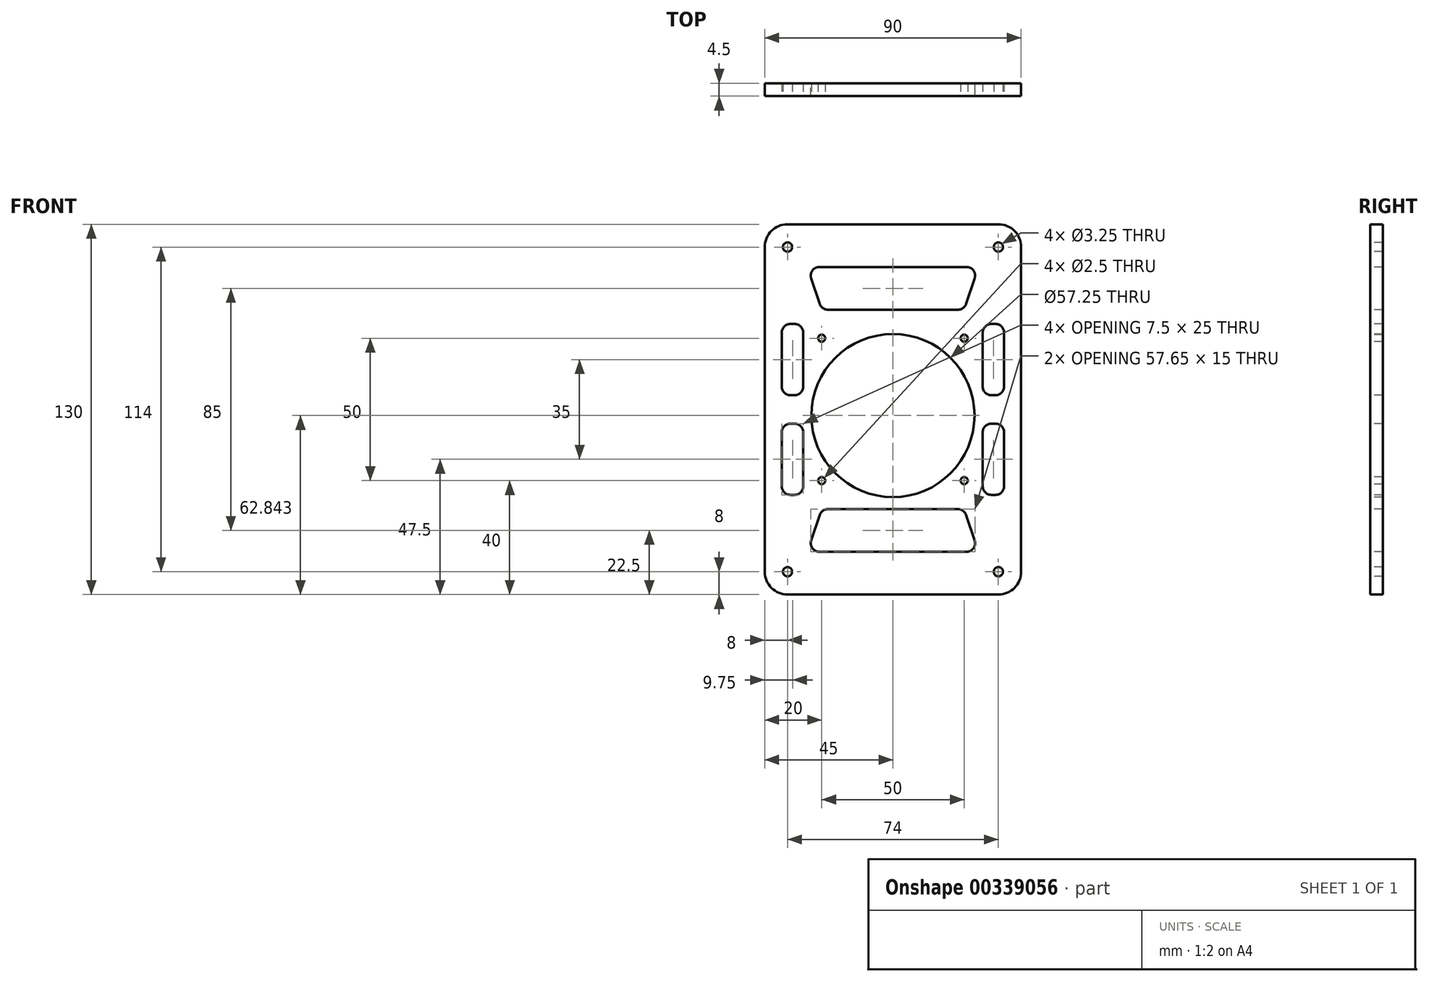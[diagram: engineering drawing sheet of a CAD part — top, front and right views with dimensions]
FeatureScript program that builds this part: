
annotation { "Feature Type Name" : "Feature", "Feature Type Description" : "" }
export const myFeature = defineFeature(function(context is Context, id is Id, definition is map)
    precondition{}
    {
        {
            var Q0;
            Q0=qCreatedBy(makeId("Front.planeOp"),FACE);
            var sketch = newSketch(context, id + "F0", { "sketchPlane" : qUnion([Q0])});
            skLineSegment(sketch, "E0.bottom", {"start": v(45, 65) * mm, "end": v(-45, 65) * mm});
            skLineSegment(sketch, "E0.top", {"start": v(45, -65) * mm, "end": v(-45, -65) * mm});
            skLineSegment(sketch, "E0.left", {"start": v(45, 65) * mm, "end": v(45, -65) * mm});
            skLineSegment(sketch, "E0.right", {"start": v(-45, 65) * mm, "end": v(-45, -65) * mm});
            skPoint(sketch, "E0.middle", {"position": v(0, 0) * mm});
            skSolve(sketch);
        }
        {
            var Q0;
            Q0=qSketchRegion(id+"F0",true);
            extrude(context, id + "F1", {"entities" : qUnion([Q0]), "oppositeDirection" : true, "depth" : 4.5 * mm});
        }
        {
            var Q0;
            Q0=makeQuery(id+"F1.opExtrude","SWEPT_EDGE",EDGE,{"disambiguationData":[OSD([sQuery(id+"F0.wireOp",EDGE,"E0.bottom"),sQuery(id+"F0.wireOp",EDGE,"E0.left")])]});
            var Q1;
            Q1=makeQuery(id+"F1.opExtrude","SWEPT_EDGE",EDGE,{"disambiguationData":[OSD([sQuery(id+"F0.wireOp",EDGE,"E0.top"),sQuery(id+"F0.wireOp",EDGE,"E0.left")])]});
            var Q2;
            Q2=makeQuery(id+"F1.opExtrude","SWEPT_EDGE",EDGE,{"disambiguationData":[OSD([sQuery(id+"F0.wireOp",EDGE,"E0.top"),sQuery(id+"F0.wireOp",EDGE,"E0.right")])]});
            var Q3;
            Q3=makeQuery(id+"F1.opExtrude","SWEPT_EDGE",EDGE,{"disambiguationData":[OSD([sQuery(id+"F0.wireOp",EDGE,"E0.bottom"),sQuery(id+"F0.wireOp",EDGE,"E0.right")])]});
            fillet(context, id + "F2", {"entities" : qUnion([Q0, Q1, Q2, Q3]), "radius" : 8 * mm, "tangentPropagation" : true, "allowEdgeOverflow" : false});
        }
        {
            var Q0;
            Q0=qCreatedBy(makeId("Front.planeOp"),FACE);
            var sketch = newSketch(context, id + "F3", { "sketchPlane" : qUnion([Q0])});
            skCircle(sketch, "E1", {"center": v(0, -2.16) * mm, "radius": 28.62 * mm});
            skSolve(sketch);
        }
        {
            var Q0;
            Q0=qSketchRegion(id+"F3",true);
            extrude(context, id + "F4", {"entities" : qUnion([Q0]), "operationType" : NewBodyOperationType.REMOVE, "endBound" : BoundingType.THROUGH_ALL, "oppositeDirection" : true, "depth" : 25.4 * mm});
        }
        {
            var Q0;
            Q0=qCreatedBy(makeId("Front.planeOp"),FACE);
            var sketch = newSketch(context, id + "F5", { "sketchPlane" : qUnion([Q0])});
            skCircle(sketch, "E2", {"center": v(-37, 57) * mm, "radius": 1.63 * mm});
            skCircle(sketch, "E3", {"center": v(37, 57) * mm, "radius": 1.62 * mm});
            skCircle(sketch, "E4", {"center": v(-37, -57) * mm, "radius": 1.62 * mm});
            skCircle(sketch, "E5", {"center": v(37, -57) * mm, "radius": 1.62 * mm});
            skSolve(sketch);
        }
        {
            var Q0;
            Q0=qSketchRegion(id+"F5",true);
            extrude(context, id + "F6", {"entities" : qUnion([Q0]), "operationType" : NewBodyOperationType.REMOVE, "endBound" : BoundingType.THROUGH_ALL, "oppositeDirection" : true, "depth" : 25.4 * mm});
        }
        {
            var Q0;
            Q0=qCreatedBy(makeId("Front.planeOp"),FACE);
            var sketch = newSketch(context, id + "F7", { "sketchPlane" : qUnion([Q0])});
            skCircle(sketch, "E6", {"center": v(-25, 25) * mm, "radius": 1.25 * mm});
            skCircle(sketch, "E7", {"center": v(25, 25) * mm, "radius": 1.25 * mm});
            skCircle(sketch, "E8", {"center": v(-25, -25) * mm, "radius": 1.25 * mm});
            skCircle(sketch, "E9", {"center": v(25, -25) * mm, "radius": 1.25 * mm});
            skSolve(sketch);
        }
        {
            var Q0;
            Q0=qSketchRegion(id+"F7",true);
            extrude(context, id + "F8", {"entities" : qUnion([Q0]), "operationType" : NewBodyOperationType.REMOVE, "endBound" : BoundingType.THROUGH_ALL, "oppositeDirection" : true, "depth" : 25.4 * mm});
        }
        {
            var Q0;
            Q0=qCreatedBy(makeId("Front.planeOp"),FACE);
            var sketch = newSketch(context, id + "F9", { "sketchPlane" : qUnion([Q0])});
            skLineSegment(sketch, "E10", {"start": v(-30, 50) * mm, "end": v(30, 50) * mm});
            skLineSegment(sketch, "E11", {"start": v(30, 50) * mm, "end": v(25, 35) * mm});
            skLineSegment(sketch, "E12", {"start": v(25, 35) * mm, "end": v(-25, 35) * mm});
            skLineSegment(sketch, "E13", {"start": v(-25, 35) * mm, "end": v(-30, 50) * mm});
            skLineSegment(sketch, "E14.bottom", {"start": v(31.5, 30) * mm, "end": v(39, 30) * mm});
            skLineSegment(sketch, "E14.top", {"start": v(31.5, 5) * mm, "end": v(39, 5) * mm});
            skLineSegment(sketch, "E14.left", {"start": v(31.5, 30) * mm, "end": v(31.5, 5) * mm});
            skLineSegment(sketch, "E14.right", {"start": v(39, 30) * mm, "end": v(39, 5) * mm});
            skLineSegment(sketch, "E15.MirrorCS", {"start": v(-39, 30) * mm, "end": v(-39, 5) * mm});
            skLineSegment(sketch, "E16.MirrorCS", {"start": v(-31.5, 30) * mm, "end": v(-31.5, 5) * mm});
            skLineSegment(sketch, "E17.MirrorCS", {"start": v(-31.5, 5) * mm, "end": v(-39, 5) * mm});
            skLineSegment(sketch, "E18.MirrorCS", {"start": v(-31.5, 30) * mm, "end": v(-39, 30) * mm});
            skLineSegment(sketch, "E19.MirrorCS", {"start": v(31.5, -5) * mm, "end": v(39, -5) * mm});
            skLineSegment(sketch, "E20.MirrorCS", {"start": v(31.5, -30) * mm, "end": v(39, -30) * mm});
            skLineSegment(sketch, "E21.MirrorCS", {"start": v(-31.5, -5) * mm, "end": v(-39, -5) * mm});
            skLineSegment(sketch, "E22.MirrorCS", {"start": v(-31.5, -30) * mm, "end": v(-39, -30) * mm});
            skLineSegment(sketch, "E23.MirrorCS", {"start": v(25, -35) * mm, "end": v(-25, -35) * mm});
            skLineSegment(sketch, "E24.MirrorCS", {"start": v(30, -50) * mm, "end": v(25, -35) * mm});
            skLineSegment(sketch, "E25.MirrorCS", {"start": v(-30, -50) * mm, "end": v(30, -50) * mm});
            skLineSegment(sketch, "E26.MirrorCS", {"start": v(-39, -30) * mm, "end": v(-39, -5) * mm});
            skLineSegment(sketch, "E27.MirrorCS", {"start": v(39, -30) * mm, "end": v(39, -5) * mm});
            skLineSegment(sketch, "E28.MirrorCS", {"start": v(31.5, -30) * mm, "end": v(31.5, -5) * mm});
            skLineSegment(sketch, "E29.MirrorCS", {"start": v(-31.5, -30) * mm, "end": v(-31.5, -5) * mm});
            skLineSegment(sketch, "E30.MirrorCS", {"start": v(-25, -35) * mm, "end": v(-30, -50) * mm});
            skSolve(sketch);
        }
        {
            var Q0;
            Q0=makeQuery(id+"F9.imprint","IMPRINT",FACE,{"disambiguationData":[TD([[makeQuery(id+"F9.imprint","IMPRINT",EDGE,{"derivedFrom":sQuery(id+"F9.wireOp",EDGE,"E10")}),-1.0]])]});
            var Q1;
            Q1=makeQuery(id+"F9.imprint","IMPRINT",FACE,{"disambiguationData":[TD([[makeQuery(id+"F9.imprint","IMPRINT",EDGE,{"derivedFrom":sQuery(id+"F9.wireOp",EDGE,"E14.bottom")}),-1.0]])]});
            var Q2;
            Q2=makeQuery(id+"F9.imprint","IMPRINT",FACE,{"disambiguationData":[TD([[makeQuery(id+"F9.imprint","IMPRINT",EDGE,{"derivedFrom":sQuery(id+"F9.wireOp",EDGE,"E19.MirrorCS")}),-1.0]])]});
            var Q3;
            Q3=makeQuery(id+"F9.imprint","IMPRINT",FACE,{"disambiguationData":[TD([[makeQuery(id+"F9.imprint","IMPRINT",EDGE,{"derivedFrom":sQuery(id+"F9.wireOp",EDGE,"E23.MirrorCS")}),1.0]])]});
            var Q4;
            Q4=makeQuery(id+"F9.imprint","IMPRINT",FACE,{"disambiguationData":[TD([[makeQuery(id+"F9.imprint","IMPRINT",EDGE,{"derivedFrom":sQuery(id+"F9.wireOp",EDGE,"E21.MirrorCS")}),1.0]])]});
            var Q5;
            Q5=makeQuery(id+"F9.imprint","IMPRINT",FACE,{"disambiguationData":[TD([[makeQuery(id+"F9.imprint","IMPRINT",EDGE,{"derivedFrom":sQuery(id+"F9.wireOp",EDGE,"E15.MirrorCS")}),1.0]])]});
            extrude(context, id + "F10", {"entities" : qUnion([Q0, Q1, Q2, Q3, Q4, Q5]), "operationType" : NewBodyOperationType.REMOVE, "endBound" : BoundingType.THROUGH_ALL, "oppositeDirection" : true, "depth" : 25.4 * mm});
        }
        {
            var Q0;
            Q0=makeQuery(id+"F10.boolean.opBoolean","COPY",EDGE,{"derivedFrom":makeQuery(id+"F10.opExtrude","SWEPT_EDGE",EDGE,{"disambiguationData":[OSD([sQuery(id+"F9.wireOp",EDGE,"E15.MirrorCS"),sQuery(id+"F9.wireOp",EDGE,"E17.MirrorCS")])]})});
            var Q1;
            Q1=makeQuery(id+"F10.boolean.opBoolean","COPY",EDGE,{"derivedFrom":makeQuery(id+"F10.opExtrude","SWEPT_EDGE",EDGE,{"disambiguationData":[OSD([sQuery(id+"F9.wireOp",EDGE,"E22.MirrorCS"),sQuery(id+"F9.wireOp",EDGE,"E26.MirrorCS")])]})});
            var Q2;
            Q2=makeQuery(id+"F10.boolean.opBoolean","COPY",EDGE,{"derivedFrom":makeQuery(id+"F10.opExtrude","SWEPT_EDGE",EDGE,{"disambiguationData":[OSD([sQuery(id+"F9.wireOp",EDGE,"E25.MirrorCS"),sQuery(id+"F9.wireOp",EDGE,"E30.MirrorCS")])]})});
            var Q3;
            Q3=makeQuery(id+"F10.boolean.opBoolean","COPY",EDGE,{"derivedFrom":makeQuery(id+"F10.opExtrude","SWEPT_EDGE",EDGE,{"disambiguationData":[OSD([sQuery(id+"F9.wireOp",EDGE,"E12"),sQuery(id+"F9.wireOp",EDGE,"E13")])]})});
            var Q4;
            Q4=makeQuery(id+"F10.boolean.opBoolean","COPY",EDGE,{"derivedFrom":makeQuery(id+"F10.opExtrude","SWEPT_EDGE",EDGE,{"disambiguationData":[OSD([sQuery(id+"F9.wireOp",EDGE,"E14.top"),sQuery(id+"F9.wireOp",EDGE,"E14.left")])]})});
            var Q5;
            Q5=makeQuery(id+"F10.boolean.opBoolean","COPY",EDGE,{"derivedFrom":makeQuery(id+"F10.opExtrude","SWEPT_EDGE",EDGE,{"disambiguationData":[OSD([sQuery(id+"F9.wireOp",EDGE,"E20.MirrorCS"),sQuery(id+"F9.wireOp",EDGE,"E28.MirrorCS")])]})});
            var Q6;
            Q6=makeQuery(id+"F10.boolean.opBoolean","COPY",EDGE,{"derivedFrom":makeQuery(id+"F10.opExtrude","SWEPT_EDGE",EDGE,{"disambiguationData":[OSD([sQuery(id+"F9.wireOp",EDGE,"E20.MirrorCS"),sQuery(id+"F9.wireOp",EDGE,"E27.MirrorCS")])]})});
            var Q7;
            Q7=makeQuery(id+"F10.boolean.opBoolean","COPY",EDGE,{"derivedFrom":makeQuery(id+"F10.opExtrude","SWEPT_EDGE",EDGE,{"disambiguationData":[OSD([sQuery(id+"F9.wireOp",EDGE,"E14.top"),sQuery(id+"F9.wireOp",EDGE,"E14.right")])]})});
            var Q8;
            Q8=makeQuery(id+"F10.boolean.opBoolean","COPY",EDGE,{"derivedFrom":makeQuery(id+"F10.opExtrude","SWEPT_EDGE",EDGE,{"disambiguationData":[OSD([sQuery(id+"F9.wireOp",EDGE,"E11"),sQuery(id+"F9.wireOp",EDGE,"E12")])]})});
            var Q9;
            Q9=makeQuery(id+"F10.boolean.opBoolean","COPY",EDGE,{"derivedFrom":makeQuery(id+"F10.opExtrude","SWEPT_EDGE",EDGE,{"disambiguationData":[OSD([sQuery(id+"F9.wireOp",EDGE,"E24.MirrorCS"),sQuery(id+"F9.wireOp",EDGE,"E25.MirrorCS")])]})});
            var Q10;
            Q10=makeQuery(id+"F10.boolean.opBoolean","COPY",EDGE,{"derivedFrom":makeQuery(id+"F10.opExtrude","SWEPT_EDGE",EDGE,{"disambiguationData":[OSD([sQuery(id+"F9.wireOp",EDGE,"E14.bottom"),sQuery(id+"F9.wireOp",EDGE,"E14.right")])]})});
            var Q11;
            Q11=makeQuery(id+"F10.boolean.opBoolean","COPY",EDGE,{"derivedFrom":makeQuery(id+"F10.opExtrude","SWEPT_EDGE",EDGE,{"disambiguationData":[OSD([sQuery(id+"F9.wireOp",EDGE,"E19.MirrorCS"),sQuery(id+"F9.wireOp",EDGE,"E27.MirrorCS")])]})});
            var Q12;
            Q12=makeQuery(id+"F10.boolean.opBoolean","COPY",EDGE,{"derivedFrom":makeQuery(id+"F10.opExtrude","SWEPT_EDGE",EDGE,{"disambiguationData":[OSD([sQuery(id+"F9.wireOp",EDGE,"E23.MirrorCS"),sQuery(id+"F9.wireOp",EDGE,"E24.MirrorCS")])]})});
            var Q13;
            Q13=makeQuery(id+"F10.boolean.opBoolean","COPY",EDGE,{"derivedFrom":makeQuery(id+"F10.opExtrude","SWEPT_EDGE",EDGE,{"disambiguationData":[OSD([sQuery(id+"F9.wireOp",EDGE,"E19.MirrorCS"),sQuery(id+"F9.wireOp",EDGE,"E28.MirrorCS")])]})});
            var Q14;
            Q14=makeQuery(id+"F10.boolean.opBoolean","COPY",EDGE,{"derivedFrom":makeQuery(id+"F10.opExtrude","SWEPT_EDGE",EDGE,{"disambiguationData":[OSD([sQuery(id+"F9.wireOp",EDGE,"E14.bottom"),sQuery(id+"F9.wireOp",EDGE,"E14.left")])]})});
            var Q15;
            Q15=makeQuery(id+"F10.boolean.opBoolean","COPY",EDGE,{"derivedFrom":makeQuery(id+"F10.opExtrude","SWEPT_EDGE",EDGE,{"disambiguationData":[OSD([sQuery(id+"F9.wireOp",EDGE,"E10"),sQuery(id+"F9.wireOp",EDGE,"E13")])]})});
            var Q16;
            Q16=makeQuery(id+"F10.boolean.opBoolean","COPY",EDGE,{"derivedFrom":makeQuery(id+"F10.opExtrude","SWEPT_EDGE",EDGE,{"disambiguationData":[OSD([sQuery(id+"F9.wireOp",EDGE,"E10"),sQuery(id+"F9.wireOp",EDGE,"E11")])]})});
            var Q17;
            Q17=makeQuery(id+"F10.boolean.opBoolean","COPY",EDGE,{"derivedFrom":makeQuery(id+"F10.opExtrude","SWEPT_EDGE",EDGE,{"disambiguationData":[OSD([sQuery(id+"F9.wireOp",EDGE,"E23.MirrorCS"),sQuery(id+"F9.wireOp",EDGE,"E30.MirrorCS")])]})});
            var Q18;
            Q18=makeQuery(id+"F10.boolean.opBoolean","COPY",EDGE,{"derivedFrom":makeQuery(id+"F10.opExtrude","SWEPT_EDGE",EDGE,{"disambiguationData":[OSD([sQuery(id+"F9.wireOp",EDGE,"E21.MirrorCS"),sQuery(id+"F9.wireOp",EDGE,"E26.MirrorCS")])]})});
            var Q19;
            Q19=makeQuery(id+"F10.boolean.opBoolean","COPY",EDGE,{"derivedFrom":makeQuery(id+"F10.opExtrude","SWEPT_EDGE",EDGE,{"disambiguationData":[OSD([sQuery(id+"F9.wireOp",EDGE,"E15.MirrorCS"),sQuery(id+"F9.wireOp",EDGE,"E18.MirrorCS")])]})});
            var Q20;
            Q20=makeQuery(id+"F10.boolean.opBoolean","COPY",EDGE,{"derivedFrom":makeQuery(id+"F10.opExtrude","SWEPT_EDGE",EDGE,{"disambiguationData":[OSD([sQuery(id+"F9.wireOp",EDGE,"E16.MirrorCS"),sQuery(id+"F9.wireOp",EDGE,"E18.MirrorCS")])]})});
            var Q21;
            Q21=makeQuery(id+"F10.boolean.opBoolean","COPY",EDGE,{"derivedFrom":makeQuery(id+"F10.opExtrude","SWEPT_EDGE",EDGE,{"disambiguationData":[OSD([sQuery(id+"F9.wireOp",EDGE,"E21.MirrorCS"),sQuery(id+"F9.wireOp",EDGE,"E29.MirrorCS")])]})});
            var Q22;
            Q22=makeQuery(id+"F10.boolean.opBoolean","COPY",EDGE,{"derivedFrom":makeQuery(id+"F10.opExtrude","SWEPT_EDGE",EDGE,{"disambiguationData":[OSD([sQuery(id+"F9.wireOp",EDGE,"E22.MirrorCS"),sQuery(id+"F9.wireOp",EDGE,"E29.MirrorCS")])]})});
            var Q23;
            Q23=makeQuery(id+"F10.boolean.opBoolean","COPY",EDGE,{"derivedFrom":makeQuery(id+"F10.opExtrude","SWEPT_EDGE",EDGE,{"disambiguationData":[OSD([sQuery(id+"F9.wireOp",EDGE,"E16.MirrorCS"),sQuery(id+"F9.wireOp",EDGE,"E17.MirrorCS")])]})});
            fillet(context, id + "F11", {"entities" : qUnion([Q0, Q1, Q2, Q3, Q4, Q5, Q6, Q7, Q8, Q9, Q10, Q11, Q12, Q13, Q14, Q15, Q16, Q17, Q18, Q19, Q20, Q21, Q22, Q23]), "radius" : 3 * mm, "tangentPropagation" : true, "allowEdgeOverflow" : false});
        }
    });
